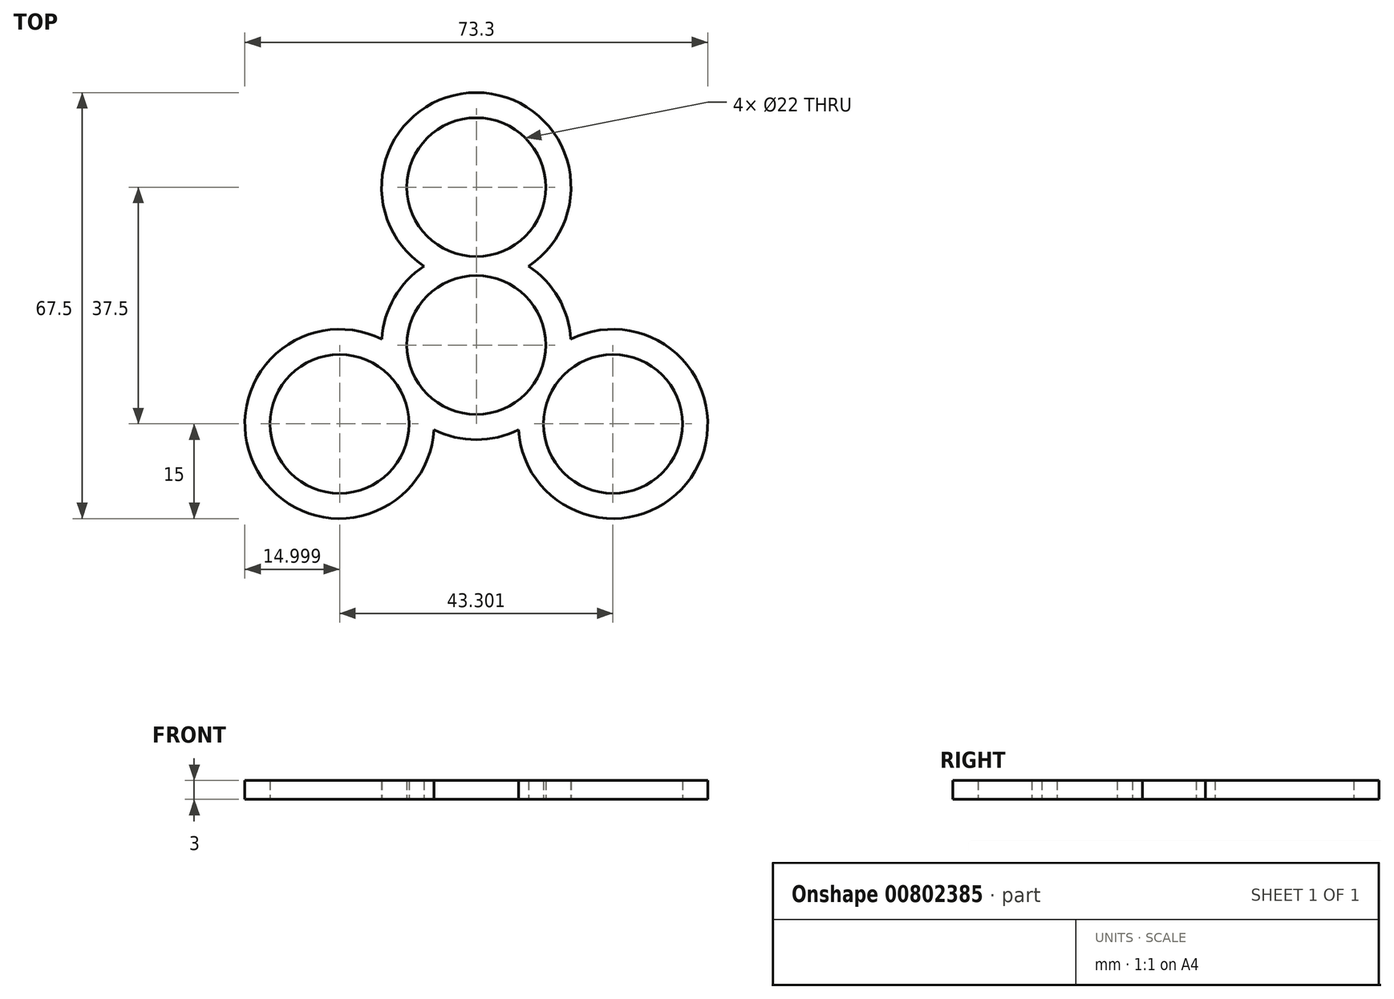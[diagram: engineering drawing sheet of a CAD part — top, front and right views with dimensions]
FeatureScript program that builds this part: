
annotation { "Feature Type Name" : "Feature", "Feature Type Description" : "" }
export const myFeature = defineFeature(function(context is Context, id is Id, definition is map)
    precondition{}
    {
        {
            var Q0;
            Q0=qCreatedBy(makeId("Top.planeOp"),FACE);
            var sketch = newSketch(context, id + "F0", { "sketchPlane" : qUnion([Q0])});
            skArc(sketch, "E0", {"start": v(9.53, 5.5) * mm, "mid": v(0, 11) * mm, "end": v(-9.53, 5.5) * mm});
            skCircle(sketch, "E1", {"center": v(0, 25) * mm, "radius": 11 * mm});
            skArc(sketch, "E2", {"start": v(8.3, 12.5) * mm, "mid": v(0, 40) * mm, "end": v(-8.3, 12.5) * mm});
            skArc(sketch, "E3", {"start": v(-8.3, 12.5) * mm, "mid": v(-10.93, 10.27) * mm, "end": v(-13, 7.5) * mm});
            skArc(sketch, "E4.trimOffspring", {"start": v(13, 7.5) * mm, "mid": v(10.93, 10.27) * mm, "end": v(8.3, 12.5) * mm});
            skArc(sketch, "E5.1.0", {"start": v(-14.97, 0.93) * mm, "mid": v(-34.64, -20) * mm, "end": v(-6.68, -13.43) * mm});
            skArc(sketch, "E5.1.1", {"start": v(-13, 7.5) * mm, "mid": v(-14.36, 4.33) * mm, "end": v(-14.97, 0.93) * mm});
            skCircle(sketch, "E5.1.2", {"center": v(-21.65, -12.5) * mm, "radius": 11 * mm});
            skArc(sketch, "E5.1.3", {"start": v(-9.53, 5.5) * mm, "mid": v(-9.53, -5.5) * mm, "end": v(0, -11) * mm});
            skArc(sketch, "E5.1.4", {"start": v(-6.68, -13.43) * mm, "mid": v(-3.43, -14.6) * mm, "end": v(0, -15) * mm});
            skArc(sketch, "E5.2.0", {"start": v(6.68, -13.43) * mm, "mid": v(34.64, -20) * mm, "end": v(14.97, 0.93) * mm});
            skArc(sketch, "E5.2.1", {"start": v(0, -15) * mm, "mid": v(3.43, -14.6) * mm, "end": v(6.68, -13.43) * mm});
            skCircle(sketch, "E5.2.2", {"center": v(21.65, -12.5) * mm, "radius": 11 * mm});
            skArc(sketch, "E5.2.3", {"start": v(0, -11) * mm, "mid": v(9.53, -5.5) * mm, "end": v(9.53, 5.5) * mm});
            skArc(sketch, "E5.2.4", {"start": v(14.97, 0.93) * mm, "mid": v(14.36, 4.33) * mm, "end": v(13, 7.5) * mm});
            skSolve(sketch);
        }
        {
            var Q0;
            Q0=makeQuery(id+"F0.imprint","IMPRINT",FACE,{"disambiguationData":[TD([[makeQuery(id+"F0.imprint","IMPRINT",EDGE,{"derivedFrom":sQuery(id+"F0.wireOp",EDGE,"E0")}),-1.0]])]});
            extrude(context, id + "F1", {"entities" : qUnion([Q0]), "depth" : 3 * mm, "offsetDistance" : 25 * mm});
        }
    });
